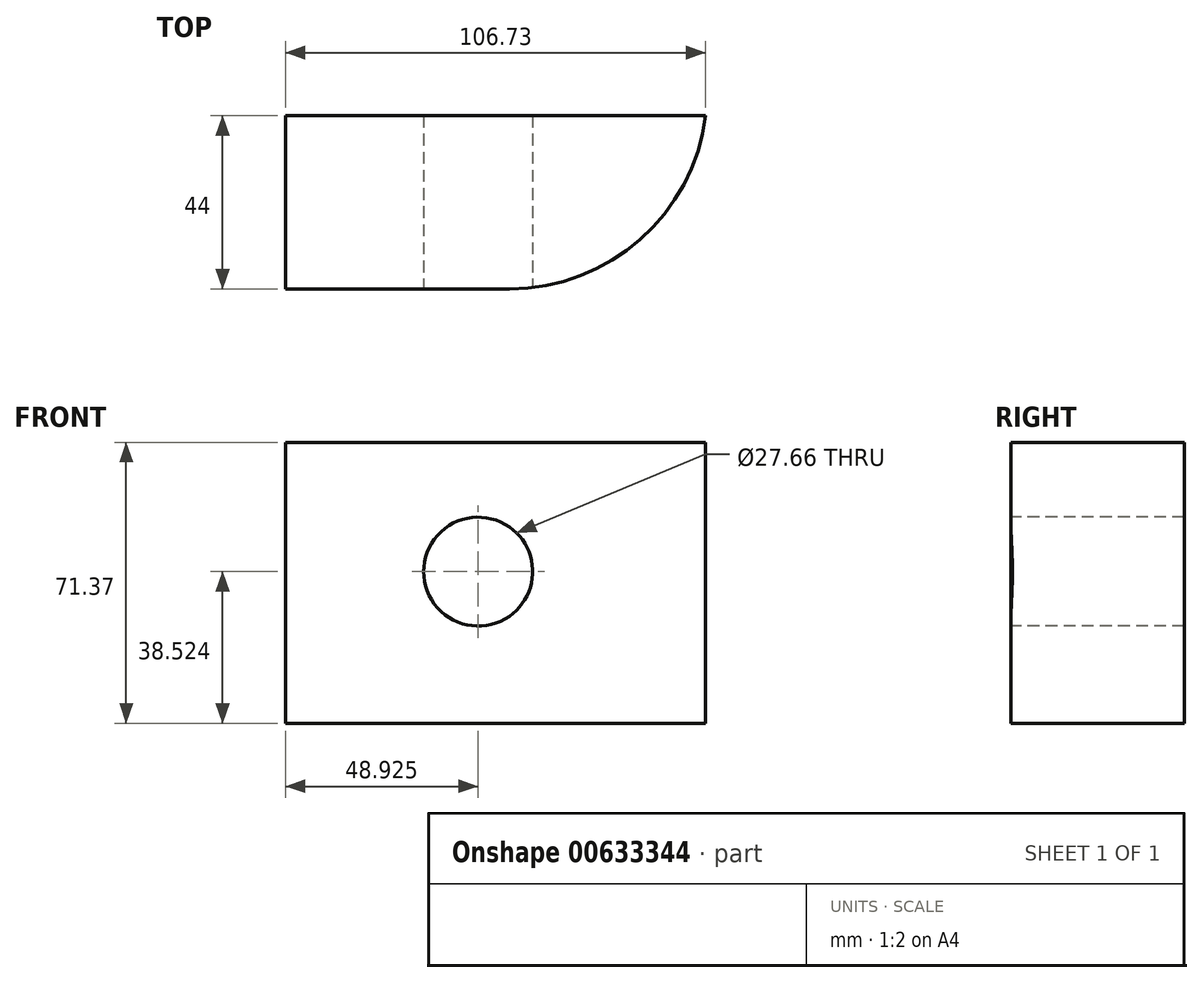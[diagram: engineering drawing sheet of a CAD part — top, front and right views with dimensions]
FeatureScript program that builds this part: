
annotation { "Feature Type Name" : "Feature", "Feature Type Description" : "" }
export const myFeature = defineFeature(function(context is Context, id is Id, definition is map)
    precondition{}
    {
        {
            var Q0;
            Q0=qCreatedBy(makeId("Top.planeOp"),FACE);
            var sketch = newSketch(context, id + "F0", { "sketchPlane" : qUnion([Q0])});
            skLineSegment(sketch, "E0.bottom", {"start": v(-42.61, 34.02) * mm, "end": v(64.12, 34.02) * mm});
            skLineSegment(sketch, "E0.top", {"start": v(-42.61, -9.98) * mm, "end": v(64.12, -9.98) * mm});
            skLineSegment(sketch, "E0.left", {"start": v(-42.61, 34.02) * mm, "end": v(-42.61, -9.98) * mm});
            skLineSegment(sketch, "E0.right", {"start": v(64.12, 34.02) * mm, "end": v(64.12, -9.98) * mm});
            skSolve(sketch);
        }
        {
            var Q0;
            Q0 = qSketchRegion(id + "F0", true);
            extrude(context, id + "F1", {"entities" : qUnion([Q0]), "depth" : 71.37 * mm, "offsetDistance" : 25.4 * mm});
        }
        {
            var Q0;
            Q0=makeQuery(id+"F1.opExtrude","SWEPT_FACE",FACE,{"disambiguationData":[OSD([sQuery(id+"F0.wireOp",EDGE,"E0.top")])]});
            var sketch = newSketch(context, id + "F2", { "sketchPlane" : qUnion([Q0])});
            skCircle(sketch, "E1", {"center": v(6.31, 38.52) * mm, "radius": 13.83 * mm});
            skSolve(sketch);
        }
        {
            var Q0;
            Q0=makeQuery(id+"F2.imprint","IMPRINT",FACE,{"disambiguationData":[TD([[makeQuery(id+"F2.imprint","IMPRINT",EDGE,{"derivedFrom":sQuery(id+"F2.wireOp",EDGE,"E1")}),1.0]])]});
            extrude(context, id + "F3", {"entities" : qUnion([Q0]), "operationType" : NewBodyOperationType.REMOVE, "endBound" : BoundingType.UP_TO_NEXT, "oppositeDirection" : true, "depth" : 25.4 * mm, "offsetDistance" : 25.4 * mm});
        }
        {
            var Q0;
            Q0=makeQuery(id+"F1.opExtrude","SWEPT_EDGE",EDGE,{"disambiguationData":[OSD([sQuery(id+"F0.wireOp",EDGE,"E0.top"),sQuery(id+"F0.wireOp",EDGE,"E0.right")])]});
            fillet(context, id + "F4", {"entities" : qUnion([Q0]), "radius" : 50.28 * mm, "tangentPropagation" : true, "allowEdgeOverflow" : false});
        }
    });
